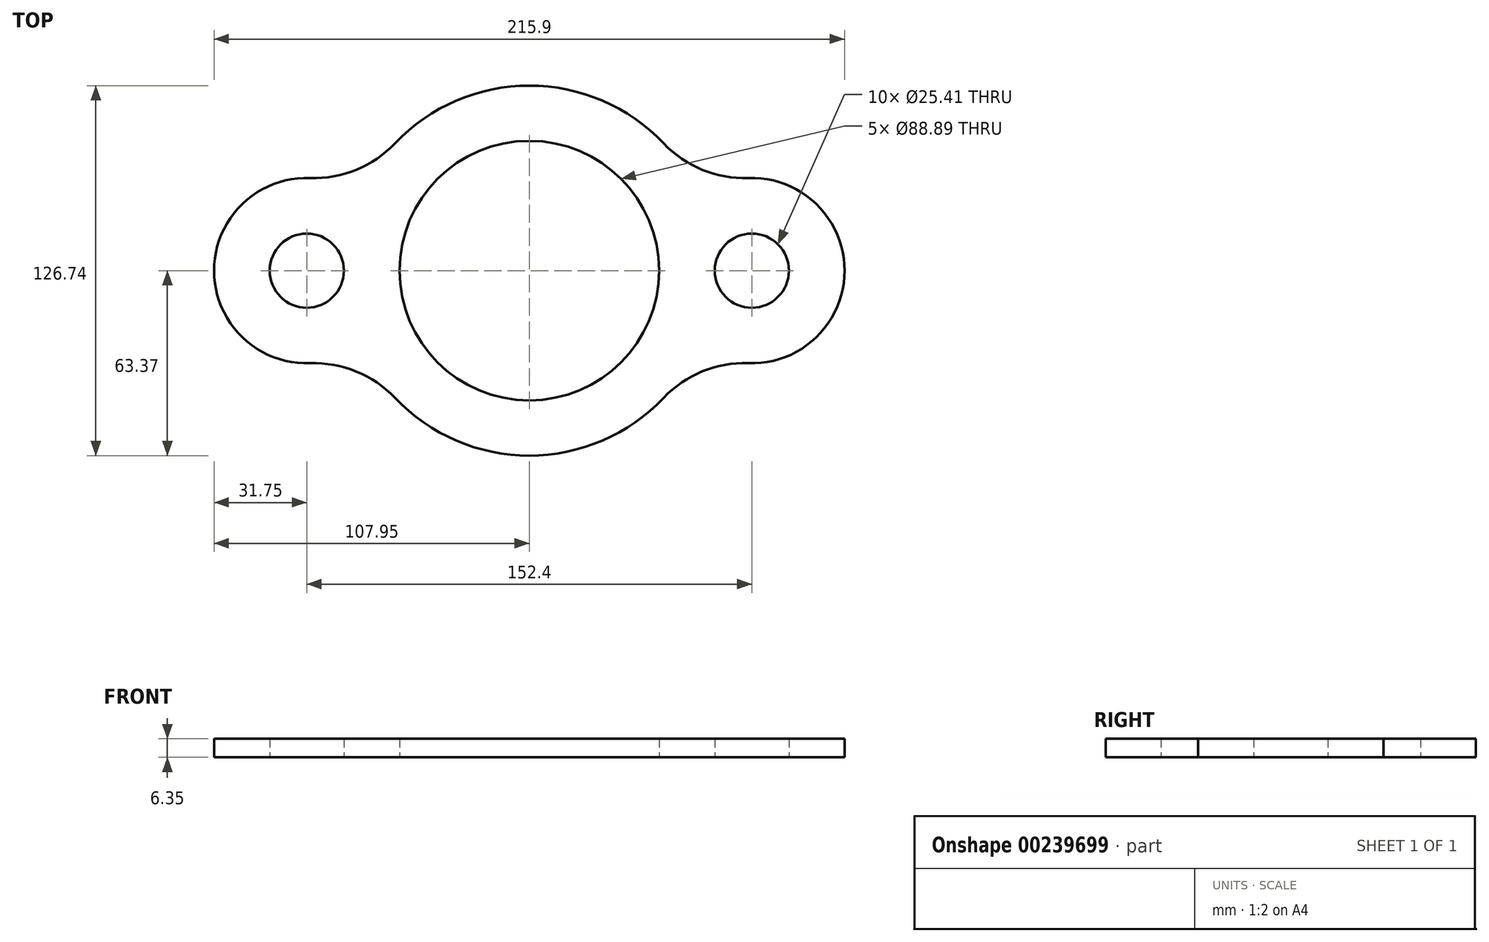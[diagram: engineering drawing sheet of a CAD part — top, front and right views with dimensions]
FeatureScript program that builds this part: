
annotation { "Feature Type Name" : "Feature", "Feature Type Description" : "" }
export const myFeature = defineFeature(function(context is Context, id is Id, definition is map)
    precondition{}
    {
        {
            var Q0;
            Q0=qCreatedBy(makeId("Top.planeOp"),FACE);
            var sketch = newSketch(context, id + "F0", { "sketchPlane" : qUnion([Q0])});
            skArc(sketch, "E0", {"start": v(-45.99, -43.6) * mm, "mid": v(0, -63.37) * mm, "end": v(46, -43.6) * mm});
            skCircle(sketch, "E1", {"center": v(0, 0) * mm, "radius": 44.44 * mm});
            skLineSegment(sketch, "E2", {"start": v(-44.44, 0) * mm, "end": v(-44.45, 0) * mm});
            skLineSegment(sketch, "E3", {"start": v(-63.5, 0) * mm, "end": v(-63.37, 0) * mm});
            skCircle(sketch, "E4", {"center": v(-76.2, 0) * mm, "radius": 12.7 * mm});
            skCircle(sketch, "E5", {"center": v(76.2, 0) * mm, "radius": 12.7 * mm});
            skArc(sketch, "E6", {"start": v(-75.04, 31.73) * mm, "mid": v(-107.95, 0) * mm, "end": v(-75.04, -31.73) * mm});
            skArc(sketch, "E7", {"start": v(75.04, -31.73) * mm, "mid": v(107.95, 0) * mm, "end": v(75.04, 31.73) * mm});
            skLineSegment(sketch, "E8.trimOffspring", {"start": v(-63.37, 0) * mm, "end": v(-63.5, 0) * mm});
            skLineSegment(sketch, "E9.trimOffspring", {"start": v(44.44, 0) * mm, "end": v(44.45, 0) * mm});
            skLineSegment(sketch, "E10.trimOffspring", {"start": v(63.37, 0) * mm, "end": v(63.5, 0) * mm});
            skPoint(sketch, "E11.visualSharp", {"position": v(-57.83, 25.9) * mm});
            skArc(sketch, "E11.filletArc", {"start": v(-75.04, 31.73) * mm, "mid": v(-59.23, 34.54) * mm, "end": v(-45.99, 43.6) * mm});
            skPoint(sketch, "E12.visualSharp", {"position": v(-57.83, -25.9) * mm});
            skArc(sketch, "E12.filletArc", {"start": v(-45.99, -43.6) * mm, "mid": v(-59.23, -34.54) * mm, "end": v(-75.04, -31.73) * mm});
            skArc(sketch, "E13.trimOffspring", {"start": v(46, 43.6) * mm, "mid": v(0, 63.37) * mm, "end": v(-45.99, 43.6) * mm});
            skPoint(sketch, "E14.visualSharp", {"position": v(57.83, 25.9) * mm});
            skArc(sketch, "E14.filletArc", {"start": v(46, 43.6) * mm, "mid": v(59.24, 34.53) * mm, "end": v(75.04, 31.73) * mm});
            skPoint(sketch, "E15.visualSharp", {"position": v(57.83, -25.9) * mm});
            skArc(sketch, "E15.filletArc", {"start": v(75.04, -31.73) * mm, "mid": v(59.24, -34.53) * mm, "end": v(46, -43.6) * mm});
            skSolve(sketch);
        }
        {
            var Q0;
            Q0=makeQuery(id+"F0.imprint","IMPRINT",FACE,{"disambiguationData":[TD([[makeQuery(id+"F0.imprint","IMPRINT",EDGE,{"derivedFrom":sQuery(id+"F0.wireOp",EDGE,"E0")}),1.0]])]});
            extrude(context, id + "F1", {"entities" : qUnion([Q0]), "depth" : 6.35 * mm});
        }
    });
